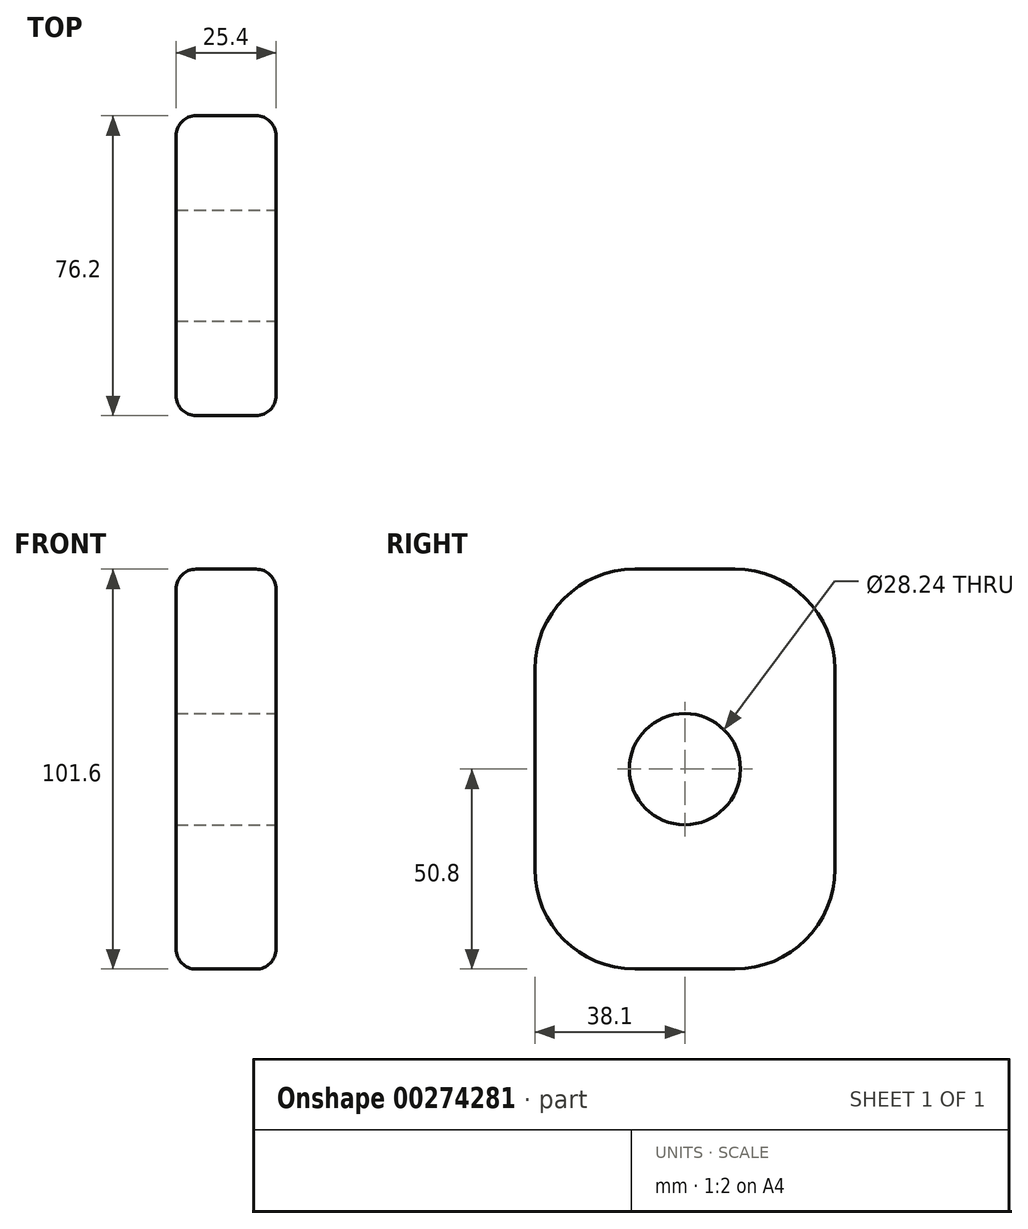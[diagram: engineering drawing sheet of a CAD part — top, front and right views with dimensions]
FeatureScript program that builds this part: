
annotation { "Feature Type Name" : "Feature", "Feature Type Description" : "" }
export const myFeature = defineFeature(function(context is Context, id is Id, definition is map)
    precondition{}
    {
        {
            var Q0;
            Q0=qCreatedBy(makeId("Right.planeOp"),FACE);
            var sketch = newSketch(context, id + "F0", { "sketchPlane" : qUnion([Q0])});
            skLineSegment(sketch, "E0.bottom", {"start": v(-38.1, 50.8) * mm, "end": v(38.1, 50.8) * mm});
            skLineSegment(sketch, "E0.top", {"start": v(-38.1, -50.8) * mm, "end": v(38.1, -50.8) * mm});
            skLineSegment(sketch, "E0.left", {"start": v(-38.1, 50.8) * mm, "end": v(-38.1, -50.8) * mm});
            skLineSegment(sketch, "E0.right", {"start": v(38.1, 50.8) * mm, "end": v(38.1, -50.8) * mm});
            skSolve(sketch);
        }
        {
            var Q0;
            Q0 = qSketchRegion(id + "F0", true);
            extrude(context, id + "F1", {"entities" : qUnion([Q0]), "depth" : 25.4 * mm});
        }
        {
            var Q0;
            Q0=makeQuery(id+"F1.opExtrude","CAP_FACE",FACE,{"disambiguationData":[OSD([sQuery(id+"F0.wireOp",EDGE,"E0.bottom"),sQuery(id+"F0.wireOp",EDGE,"E0.top"),sQuery(id+"F0.wireOp",EDGE,"E0.left"),sQuery(id+"F0.wireOp",EDGE,"E0.right")])],"isStart":false});
            var sketch = newSketch(context, id + "F2", { "sketchPlane" : qUnion([Q0])});
            skCircle(sketch, "E1", {"center": v(0, 0) * mm, "radius": 14.12 * mm});
            skSolve(sketch);
        }
        {
            var Q0;
            Q0 = qSketchRegion(id + "F2", true);
            extrude(context, id + "F3", {"entities" : qUnion([Q0]), "operationType" : NewBodyOperationType.REMOVE, "oppositeDirection" : true, "depth" : 25.4 * mm});
        }
        {
            var Q0;
            Q0=makeQuery(id+"F1.opExtrude","SWEPT_EDGE",EDGE,{"disambiguationData":[OSD([sQuery(id+"F0.wireOp",EDGE,"E0.bottom"),sQuery(id+"F0.wireOp",EDGE,"E0.left")])]});
            var Q1;
            Q1=makeQuery(id+"F1.opExtrude","SWEPT_EDGE",EDGE,{"disambiguationData":[OSD([sQuery(id+"F0.wireOp",EDGE,"E0.top"),sQuery(id+"F0.wireOp",EDGE,"E0.left")])]});
            var Q2;
            Q2=makeQuery(id+"F1.opExtrude","SWEPT_EDGE",EDGE,{"disambiguationData":[OSD([sQuery(id+"F0.wireOp",EDGE,"E0.bottom"),sQuery(id+"F0.wireOp",EDGE,"E0.right")])]});
            var Q3;
            Q3=makeQuery(id+"F1.opExtrude","SWEPT_EDGE",EDGE,{"disambiguationData":[OSD([sQuery(id+"F0.wireOp",EDGE,"E0.top"),sQuery(id+"F0.wireOp",EDGE,"E0.right")])]});
            fillet(context, id + "F4", {"entities" : qUnion([Q0, Q1, Q2, Q3]), "radius" : 25.4 * mm, "tangentPropagation" : true, "allowEdgeOverflow" : false});
        }
        {
            var Q0;
            Q0=makeQuery(id+"F1.opExtrude","CAP_EDGE",EDGE,{"disambiguationData":[OSD([sQuery(id+"F0.wireOp",EDGE,"E0.right")])],"isStart":false});
            var Q1;
            Q1=makeQuery(id+"F1.opExtrude","CAP_EDGE",EDGE,{"disambiguationData":[OSD([sQuery(id+"F0.wireOp",EDGE,"E0.right")])],"isStart":true});
            fillet(context, id + "F5", {"entities" : qUnion([Q0, Q1]), "radius" : 5.08 * mm, "tangentPropagation" : true, "allowEdgeOverflow" : false});
        }
    });
